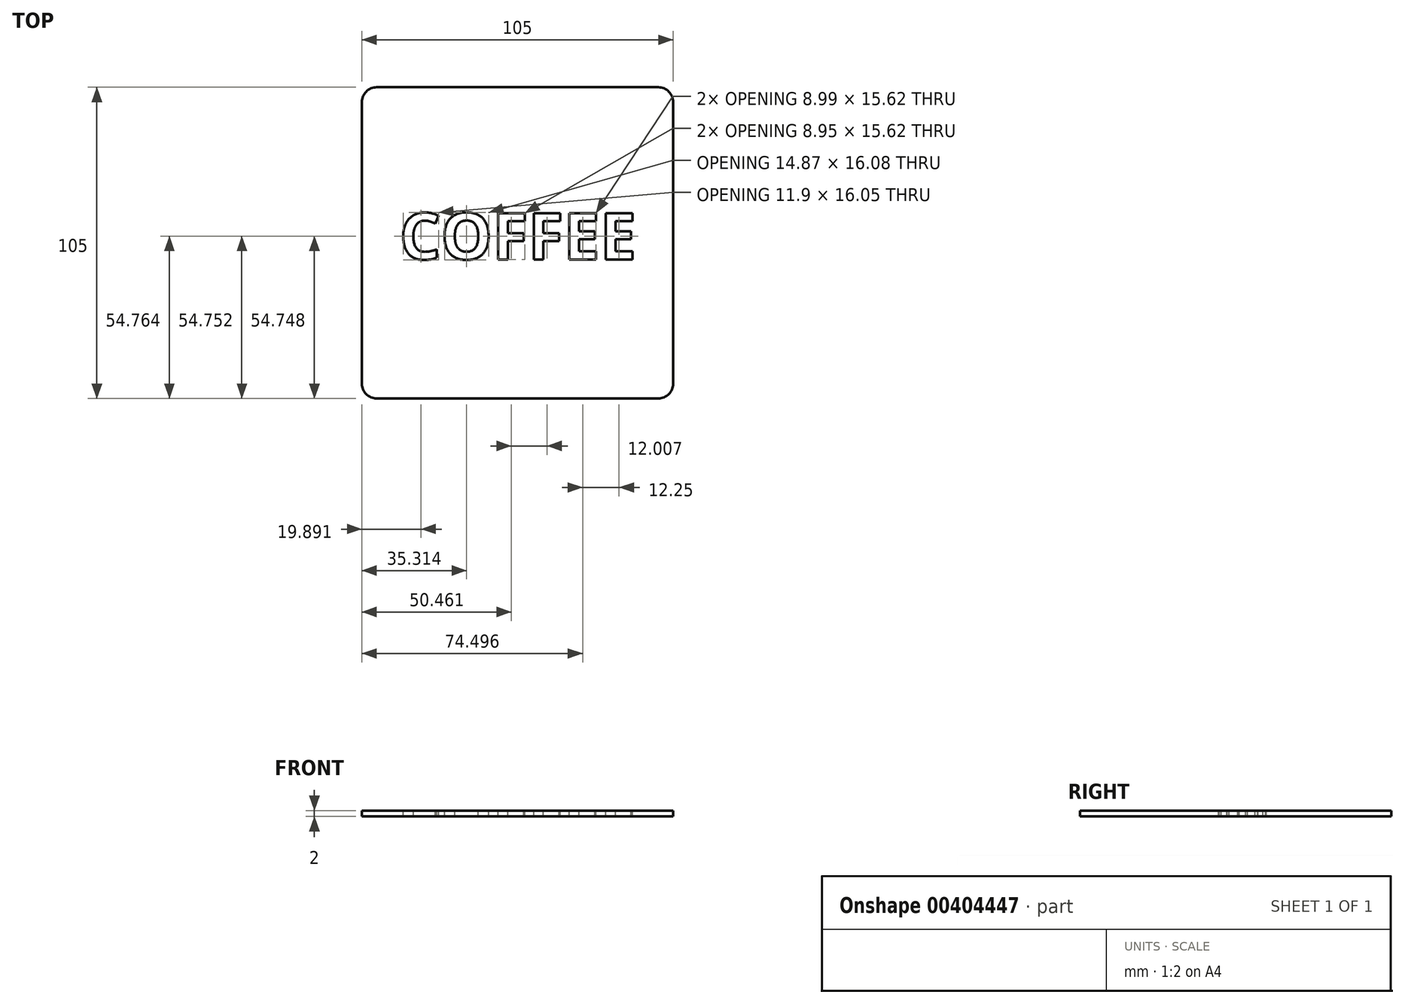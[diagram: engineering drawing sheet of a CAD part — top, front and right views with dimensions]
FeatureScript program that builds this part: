
annotation { "Feature Type Name" : "Feature", "Feature Type Description" : "" }
export const myFeature = defineFeature(function(context is Context, id is Id, definition is map)
    precondition{}
    {
        {
            var Q0;
            Q0=qCreatedBy(makeId("Top.planeOp"),FACE);
            var sketch = newSketch(context, id + "F0", { "sketchPlane" : qUnion([Q0])});
            skLineSegment(sketch, "E0.bottom", {"start": v(47.5, -52.5) * mm, "end": v(-47.5, -52.5) * mm});
            skLineSegment(sketch, "E0.top", {"start": v(47.5, 52.5) * mm, "end": v(-47.5, 52.5) * mm});
            skLineSegment(sketch, "E0.left", {"start": v(52.5, -47.5) * mm, "end": v(52.5, 47.5) * mm});
            skLineSegment(sketch, "E0.right", {"start": v(-52.5, -47.5) * mm, "end": v(-52.5, 47.5) * mm});
            skPoint(sketch, "E0.middle", {"position": v(0, 0) * mm});
            skPoint(sketch, "E1", {"position": v(-52.5, 47.5) * mm});
            skPoint(sketch, "E2", {"position": v(-47.5, 52.5) * mm});
            skPoint(sketch, "E3", {"position": v(47.5, 52.5) * mm});
            skPoint(sketch, "E4", {"position": v(52.5, 47.5) * mm});
            skPoint(sketch, "E5", {"position": v(52.5, -47.5) * mm});
            skPoint(sketch, "E6", {"position": v(47.5, -52.5) * mm});
            skPoint(sketch, "E7", {"position": v(-52.5, -47.5) * mm});
            skPoint(sketch, "E8", {"position": v(-47.5, -52.5) * mm});
            skArc(sketch, "E9", {"start": v(-47.5, 52.5) * mm, "mid": v(-51.04, 51.04) * mm, "end": v(-52.5, 47.5) * mm});
            skArc(sketch, "E10", {"start": v(52.5, 47.5) * mm, "mid": v(51.04, 51.04) * mm, "end": v(47.5, 52.5) * mm});
            skArc(sketch, "E11", {"start": v(-52.5, -47.5) * mm, "mid": v(-51.04, -51.04) * mm, "end": v(-47.5, -52.5) * mm});
            skArc(sketch, "E12", {"start": v(47.5, -52.5) * mm, "mid": v(51.04, -51.04) * mm, "end": v(52.5, -47.5) * mm});
            skPoint(sketch, "E13.orphan", {"position": v(-52.5, 52.5) * mm});
            skPoint(sketch, "E14.orphan", {"position": v(52.5, 52.5) * mm});
            skPoint(sketch, "E15.orphan", {"position": v(52.5, -52.5) * mm});
            skPoint(sketch, "E16.orphan", {"position": v(-52.5, -52.5) * mm});
            skSolve(sketch);
        }
        {
            var Q0;
            Q0=qSketchRegion(id+"F0",true);
            extrude(context, id + "F1", {"entities" : qUnion([Q0]), "depth" : 2 * mm});
        }
        {
            var Q0;
            Q0=makeQuery(id+"F1.opExtrude","CAP_FACE",FACE,{"disambiguationData":[OSD([sQuery(id+"F0.wireOp",EDGE,"E0.bottom"),sQuery(id+"F0.wireOp",EDGE,"E0.top"),sQuery(id+"F0.wireOp",EDGE,"E0.left"),sQuery(id+"F0.wireOp",EDGE,"E0.right"),sQuery(id+"F0.wireOp",EDGE,"E9"),sQuery(id+"F0.wireOp",EDGE,"E10"),sQuery(id+"F0.wireOp",EDGE,"E11"),sQuery(id+"F0.wireOp",EDGE,"E12")])],"isStart":false});
            var sketch = newSketch(context, id + "F2", { "sketchPlane" : qUnion([Q0])});
            skText(sketch, "E17", { "text": "COFFEE", "fontName": "OpenSans-Bold.ttf"});
            const initialGuessF2  = {"E17": [-0.03983, -0.00556, 1, 0, 0.01575]};
            skSetInitialGuess(sketch, initialGuessF2);
            skSolve(sketch);
        }
        {
            var Q0;
            Q0=qSketchRegion(id+"F2",true);
            extrude(context, id + "F3", {"entities" : qUnion([Q0]), "operationType" : NewBodyOperationType.REMOVE, "oppositeDirection" : true, "depth" : 30 * mm});
        }
    });
